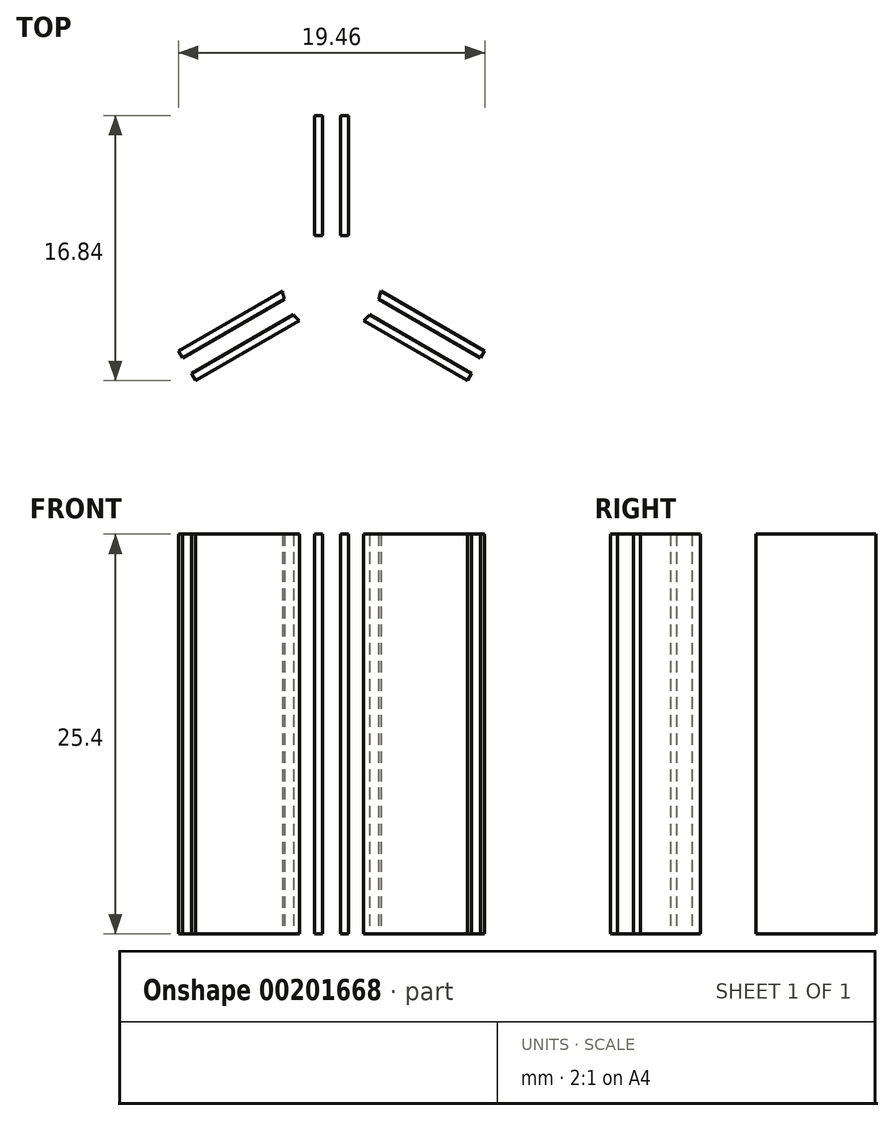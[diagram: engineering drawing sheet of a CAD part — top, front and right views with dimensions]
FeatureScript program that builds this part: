
annotation { "Feature Type Name" : "Feature", "Feature Type Description" : "" }
export const myFeature = defineFeature(function(context is Context, id is Id, definition is map)
    precondition{}
    {
        {
            var Q0;
            Q0=qCreatedBy(makeId("Top.planeOp"),FACE);
            var sketch = newSketch(context, id + "F0", { "sketchPlane" : qUnion([Q0])});
            skCircle(sketch, "E0", {"center": v(0, 0) * mm, "radius": 3.18 * mm});
            skLineSegment(sketch, "E1.bottom", {"start": v(-1.09, 2.98) * mm, "end": v(1.09, 2.98) * mm});
            skLineSegment(sketch, "E1.top", {"start": v(-1.09, 10.6) * mm, "end": v(1.09, 10.6) * mm});
            skLineSegment(sketch, "E1.left", {"start": v(-1.09, 2.98) * mm, "end": v(-1.09, 10.6) * mm});
            skLineSegment(sketch, "E1.right", {"start": v(1.09, 2.98) * mm, "end": v(1.09, 10.6) * mm});
            skLineSegment(sketch, "E2.bottom", {"start": v(-0.57, 10.6) * mm, "end": v(0.57, 10.6) * mm});
            skLineSegment(sketch, "E2.top", {"start": v(-0.57, 2.98) * mm, "end": v(0.57, 2.98) * mm});
            skLineSegment(sketch, "E2.left", {"start": v(-0.57, 10.6) * mm, "end": v(-0.57, 2.98) * mm});
            skLineSegment(sketch, "E2.right", {"start": v(0.57, 10.6) * mm, "end": v(0.57, 2.98) * mm});
            skPoint(sketch, "E3", {"position": v(0, 10.6) * mm});
            skLineSegment(sketch, "E4.1.0", {"start": v(-2.04, -2.43) * mm, "end": v(-8.64, -6.24) * mm});
            skLineSegment(sketch, "E4.1.1", {"start": v(-8.9, -5.8) * mm, "end": v(-2.3, -1.99) * mm});
            skLineSegment(sketch, "E4.1.2", {"start": v(-9.47, -4.8) * mm, "end": v(-2.87, -1) * mm});
            skLineSegment(sketch, "E4.1.3", {"start": v(-3.13, -0.55) * mm, "end": v(-9.73, -4.36) * mm});
            skLineSegment(sketch, "E4.1.4", {"start": v(-8.64, -6.24) * mm, "end": v(-9.73, -4.36) * mm});
            skLineSegment(sketch, "E4.2.0", {"start": v(3.13, -0.55) * mm, "end": v(9.73, -4.36) * mm});
            skLineSegment(sketch, "E4.2.1", {"start": v(9.47, -4.8) * mm, "end": v(2.87, -1) * mm});
            skLineSegment(sketch, "E4.2.2", {"start": v(8.9, -5.8) * mm, "end": v(2.3, -1.99) * mm});
            skLineSegment(sketch, "E4.2.3", {"start": v(2.04, -2.43) * mm, "end": v(8.64, -6.24) * mm});
            skLineSegment(sketch, "E4.2.4", {"start": v(9.73, -4.36) * mm, "end": v(8.64, -6.24) * mm});
            skSolve(sketch);
        }
        {
            var Q0;
            {var subQ0=sQuery(id+"F0.wireOp",EDGE,"E1.right");Q0=makeQuery(id+"F0.imprint","IMPRINT",FACE,{"disambiguationData":[TD([[makeQuery(id+"F0.imprint","IMPRINT",EDGE,{"derivedFrom":subQ0}),1.0]])]});}
            var Q1;
            {var subQ0=sQuery(id+"F0.wireOp",EDGE,"E1.left");Q1=makeQuery(id+"F0.imprint","IMPRINT",FACE,{"disambiguationData":[TD([[makeQuery(id+"F0.imprint","IMPRINT",EDGE,{"derivedFrom":subQ0}),-1.0]])]});}
            var Q2;
            {var subQ0=sQuery(id+"F0.wireOp",EDGE,"E4.1.3");Q2=makeQuery(id+"F0.imprint","IMPRINT",FACE,{"disambiguationData":[TD([[makeQuery(id+"F0.imprint","IMPRINT",EDGE,{"derivedFrom":subQ0}),1.0]])]});}
            var Q3;
            {var subQ0=sQuery(id+"F0.wireOp",EDGE,"E4.1.0");Q3=makeQuery(id+"F0.imprint","IMPRINT",FACE,{"disambiguationData":[TD([[makeQuery(id+"F0.imprint","IMPRINT",EDGE,{"derivedFrom":subQ0}),-1.0]])]});}
            var Q4;
            {var subQ0=sQuery(id+"F0.wireOp",EDGE,"E4.2.3");Q4=makeQuery(id+"F0.imprint","IMPRINT",FACE,{"disambiguationData":[TD([[makeQuery(id+"F0.imprint","IMPRINT",EDGE,{"derivedFrom":subQ0}),1.0]])]});}
            var Q5;
            {var subQ0=sQuery(id+"F0.wireOp",EDGE,"E4.2.0");Q5=makeQuery(id+"F0.imprint","IMPRINT",FACE,{"disambiguationData":[TD([[makeQuery(id+"F0.imprint","IMPRINT",EDGE,{"derivedFrom":subQ0}),-1.0]])]});}
            var Q6;
            {var subQ1=sQuery(id+"F0.wireOp",EDGE,"E0");var subQ3=sQuery(id+"F0.wireOp",EDGE,"E2.right");var subQ4=makeQuery(id+"F0.imprint","INTERSECT",VERTEX,{"derivedFrom":[subQ1,subQ3]});Q6=makeQuery(id+"F0.imprint","IMPRINT",FACE,{"disambiguationData":[TD([[makeQuery(id+"F0.imprint","IMPRINT",EDGE,{"disambiguationData":[TD([[subQ4,1.0]])],"derivedFrom":subQ1}),1.0]])]});}
            var Q7;
            {var subQ1=sQuery(id+"F0.wireOp",EDGE,"E0");var subQ3=sQuery(id+"F0.wireOp",EDGE,"E2.left");var subQ4=makeQuery(id+"F0.imprint","INTERSECT",VERTEX,{"derivedFrom":[subQ1,subQ3]});Q7=makeQuery(id+"F0.imprint","IMPRINT",FACE,{"disambiguationData":[TD([[makeQuery(id+"F0.imprint","IMPRINT",EDGE,{"disambiguationData":[TD([[subQ4,-1.0]])],"derivedFrom":subQ1}),1.0]])]});}
            var Q8;
            {var subQ10=sQuery(id+"F0.wireOp",EDGE,"E2.top");Q8=makeQuery(id+"F0.imprint","IMPRINT",FACE,{"disambiguationData":[TD([[makeQuery(id+"F0.imprint","IMPRINT",EDGE,{"derivedFrom":subQ10}),-1.0]])]});}
            extrude(context, id + "F1", {"entities" : qUnion([Q0, Q1, Q2, Q3, Q4, Q5, Q6, Q7, Q8]), "depth" : 25.4 * mm});
        }
    });
